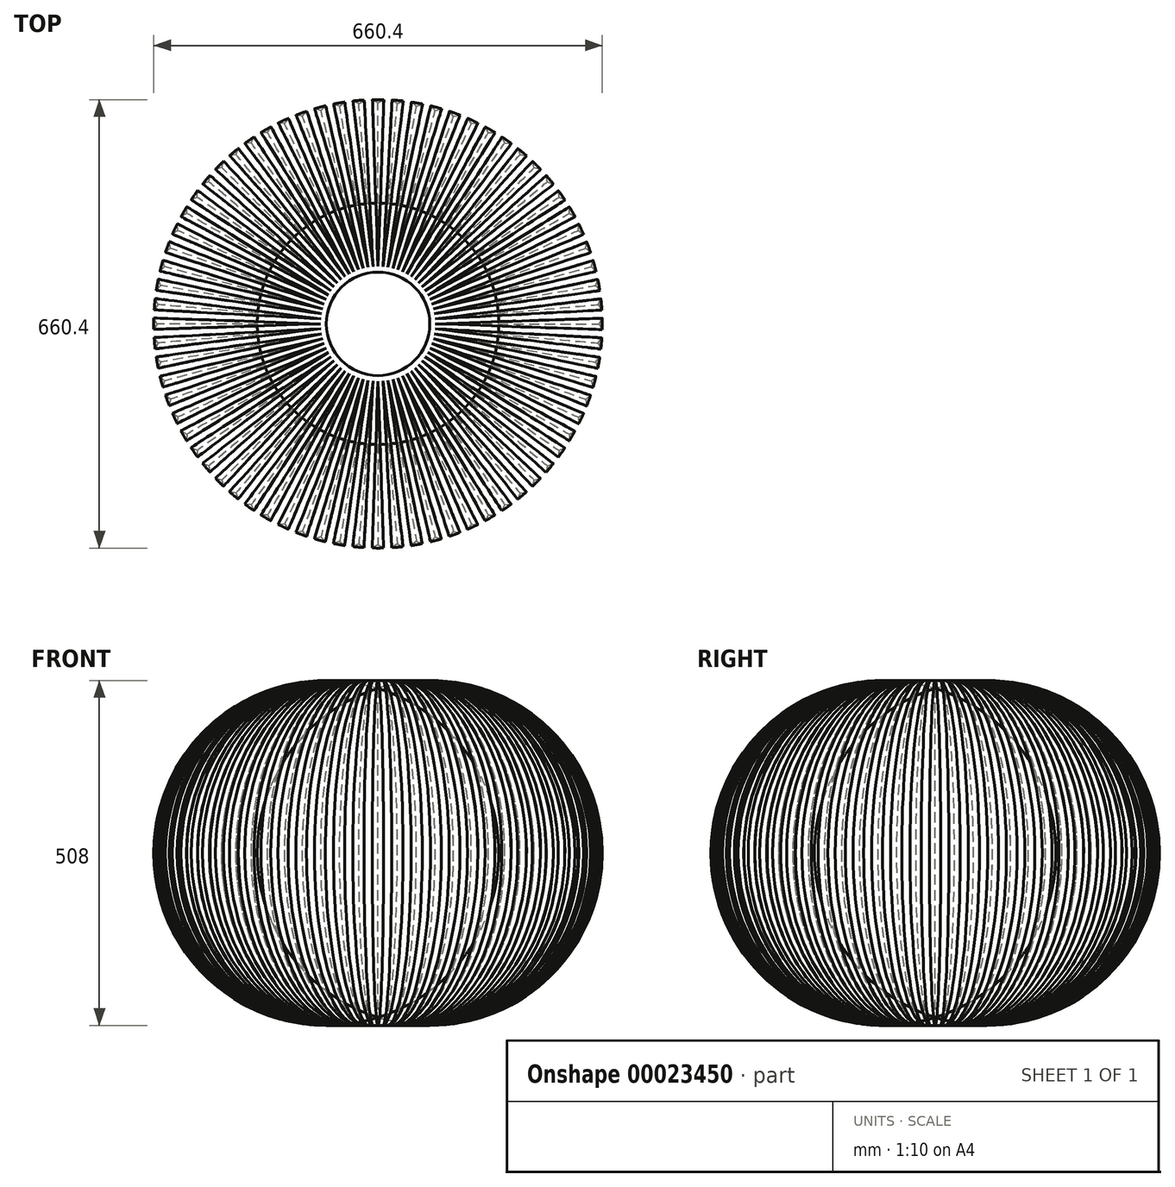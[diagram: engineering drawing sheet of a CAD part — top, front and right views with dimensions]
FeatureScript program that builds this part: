
annotation { "Feature Type Name" : "Feature", "Feature Type Description" : "" }
export const myFeature = defineFeature(function(context is Context, id is Id, definition is map)
    precondition{}
    {
        {
            var Q0;
            Q0=qCreatedBy(makeId("Front.planeOp"),FACE);
            var sketch = newSketch(context, id + "F0", { "sketchPlane" : qUnion([Q0])});
            skLineSegment(sketch, "E0", {"start": v(0, 492.91) * mm, "end": v(0, -560.81) * mm, "construction": true});
            skLineSegment(sketch, "E1.bottom", {"start": v(0, 254) * mm, "end": v(-76.2, 254) * mm});
            skLineSegment(sketch, "E1.top", {"start": v(0, -254) * mm, "end": v(-76.2, -254) * mm});
            skLineSegment(sketch, "E1.left", {"start": v(0, 254) * mm, "end": v(0, -254) * mm});
            skLineSegment(sketch, "E1.right", {"start": v(-76.2, 254) * mm, "end": v(-76.2, -254) * mm});
            skArc(sketch, "E2", {"start": v(-76.2, 254) * mm, "mid": v(-330.2, 0) * mm, "end": v(-76.2, -254) * mm});
            skSolve(sketch);
        }
        {
            var Q0;
            Q0=makeQuery(id+"F0.imprint","IMPRINT",FACE,{"disambiguationData":[TD([[makeQuery(id+"F0.imprint","IMPRINT",EDGE,{"derivedFrom":sQuery(id+"F0.wireOp",EDGE,"E1.right")}),-1.0]])]});
            var Q1;
            Q1=makeQuery(id+"F0.imprint","IMPRINT",FACE,{"disambiguationData":[TD([[makeQuery(id+"F0.imprint","IMPRINT",EDGE,{"derivedFrom":sQuery(id+"F0.wireOp",EDGE,"E1.bottom")}),1.0]])]});
            var Q2;
            Q2=sQuery(id+"F0.wireOp",EDGE,"E0");
            revolve(context, id + "F1", {"entities" : qUnion([Q0, Q1]), "axis" : qUnion([Q2]), "revolveType" : RevolveType.FULL});
        }
        {
            var Q0;
            Q0=qCreatedBy(makeId("Front.planeOp"),FACE);
            var sketch = newSketch(context, id + "F2", { "sketchPlane" : qUnion([Q0])});
            skLineSegment(sketch, "E3", {"start": v(0, 760) * mm, "end": v(0, -293.71) * mm, "construction": true});
            skLineSegment(sketch, "E4.bottom", {"start": v(0, 254) * mm, "end": v(-76.2, 254) * mm});
            skLineSegment(sketch, "E4.top", {"start": v(0, -254) * mm, "end": v(-76.2, -254) * mm});
            skLineSegment(sketch, "E4.left", {"start": v(0, 254) * mm, "end": v(0, -254) * mm});
            skLineSegment(sketch, "E4.right", {"start": v(-76.2, 254) * mm, "end": v(-76.2, -254) * mm});
            skArc(sketch, "E5", {"start": v(-76.2, 254) * mm, "mid": v(-330.2, 0) * mm, "end": v(-76.2, -254) * mm});
            skArc(sketch, "E6", {"start": v(-76.2, 254) * mm, "mid": v(-325.12, 0) * mm, "end": v(-76.2, -254) * mm});
            skLineSegment(sketch, "E7", {"start": v(-71.07, 0) * mm, "end": v(-76.2, -254) * mm, "construction": true});
            skSolve(sketch);
        }
        {
            var Q0;
            Q0=sQuery(id+"F2.wireOp",EDGE,"E4.right");
            cPlane(context, id + "F3", {"entities" : qUnion([Q0]), "cplaneType" : CPlaneType.LINE_ANGLE, "offset" : 152.4 * mm, "angle" : 180 * degree, "width" : 152.4 * mm, "height" : 152.4 * mm});
        }
        {
            var Q0;
            Q0=qCreatedBy(id+"F3.planeOp",FACE);
            var sketch = newSketch(context, id + "F4", { "sketchPlane" : qUnion([Q0])});
            skLineSegment(sketch, "E8", {"start": v(16.43, -254) * mm, "end": v(0, -254) * mm});
            skLineSegment(sketch, "E9", {"start": v(0, -254) * mm, "end": v(0, -244.51) * mm});
            skLineSegment(sketch, "E10", {"start": v(0, -244.51) * mm, "end": v(0, -254) * mm});
            skLineSegment(sketch, "E11", {"start": v(0, -254) * mm, "end": v(0, -261.75) * mm, "construction": true});
            skLineSegment(sketch, "E12", {"start": v(16.43, -254) * mm, "end": v(-17.03, -254.34) * mm});
            skLineSegment(sketch, "E13", {"start": v(15.24, -262.76) * mm, "end": v(0, -254.17) * mm});
            skLineSegment(sketch, "E14", {"start": v(0, -254.17) * mm, "end": v(0, -254) * mm});
            skLineSegment(sketch, "E15", {"start": v(-15.24, -263.18) * mm, "end": v(0, -254.17) * mm});
            skLineSegment(sketch, "E16", {"start": v(-15.24, -263.18) * mm, "end": v(15.24, -262.76) * mm});
            skSolve(sketch);
        }
        {
            var Q0;
            Q0=makeQuery(id+"F4.imprint","IMPRINT",FACE,{"disambiguationData":[TD([[makeQuery(id+"F4.imprint","IMPRINT",EDGE,{"derivedFrom":sQuery(id+"F4.wireOp",EDGE,"E13")}),1.0]])]});
            var Q1;
            Q1=sQuery(id+"F2.wireOp",EDGE,"E6");
            sweep(context, id + "F5", {"operationType" : NewBodyOperationType.REMOVE, "profiles" : qUnion([Q0]), "path" : qUnion([Q1])});
        }
        {
            var Q0;
            Q0=makeQuery(id+"F5.boolean.opBoolean","COPY",FACE,{"derivedFrom":makeQuery(id+"F5.opSweep","SWEPT_FACE",FACE,{"disambiguationData":[OSD([sQuery(id+"F2.wireOp",EDGE,"E6"),sQuery(id+"F4.wireOp",EDGE,"E15")])]})});
            var Q1;
            Q1=makeQuery(id+"F5.boolean.opBoolean","COPY",FACE,{"derivedFrom":makeQuery(id+"F5.opSweep","SWEPT_FACE",FACE,{"disambiguationData":[OSD([sQuery(id+"F2.wireOp",EDGE,"E6"),sQuery(id+"F4.wireOp",EDGE,"E13")])]})});
            var Q2;
            Q2=sQuery(id+"F0.wireOp",EDGE,"E0");
            circularPattern(context, id + "F6", {"faces" : qUnion([Q0, Q1]), "axis" : qUnion([Q2]), "angle" : 360 * degree, "instanceCount" : 72, "equalSpace" : true, "patternType" : PatternType.FACE});
        }
    });
